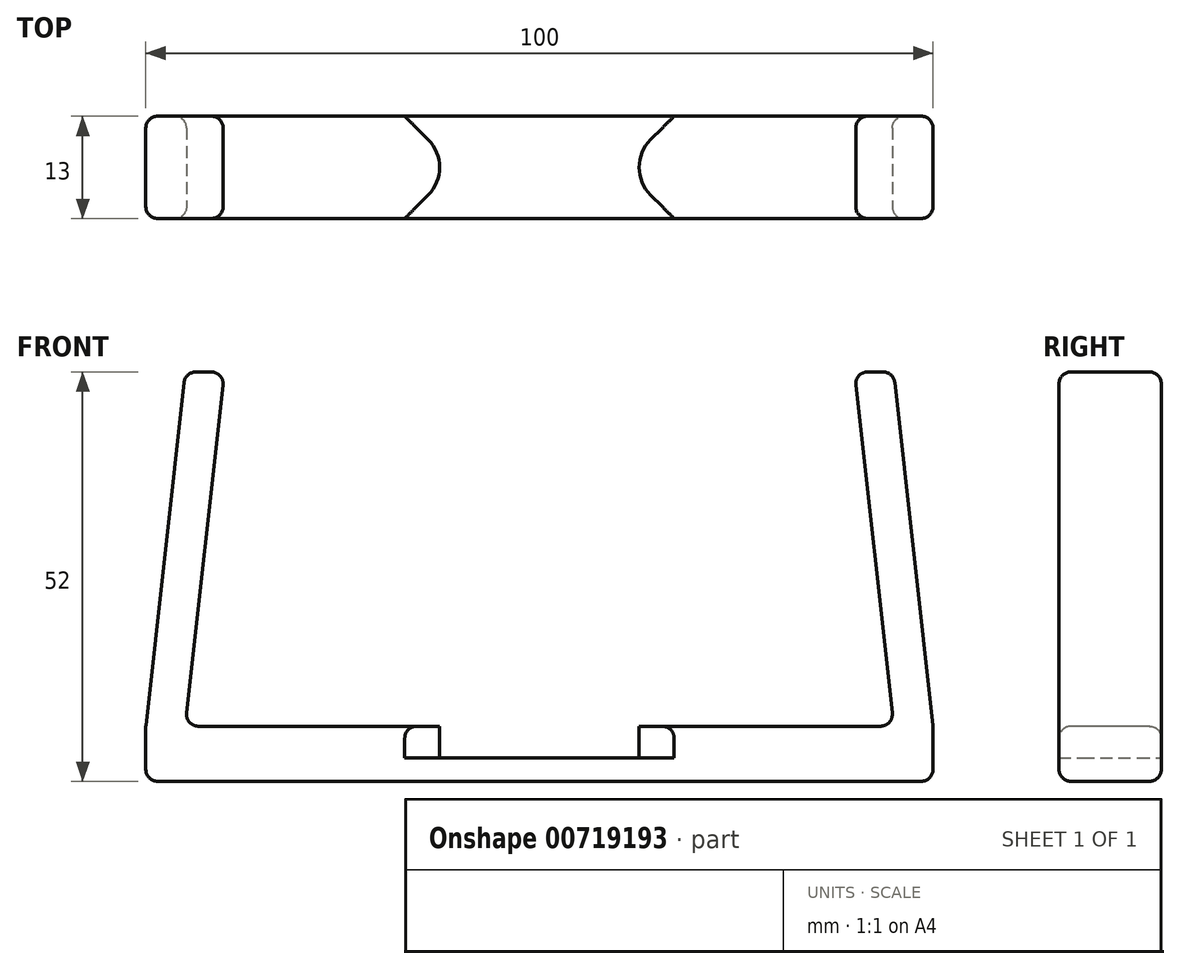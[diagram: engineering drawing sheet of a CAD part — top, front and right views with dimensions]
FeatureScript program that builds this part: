
annotation { "Feature Type Name" : "Feature", "Feature Type Description" : "" }
export const myFeature = defineFeature(function(context is Context, id is Id, definition is map)
    precondition{}
    {
        {
            var Q0;
            Q0=qCreatedBy(makeId("Top.planeOp"),FACE);
            var sketch = newSketch(context, id + "F0", { "sketchPlane" : qUnion([Q0])});
            skLineSegment(sketch, "E0", {"start": v(-45, 0) * mm, "end": v(0, 0) * mm});
            skLineSegment(sketch, "E1", {"start": v(0, 0) * mm, "end": v(45, 0) * mm});
            skLineSegment(sketch, "E2", {"start": v(45, 7) * mm, "end": v(-45, 7) * mm});
            skLineSegment(sketch, "E3", {"start": v(-45, 0) * mm, "end": v(-40, -45) * mm});
            skLineSegment(sketch, "E4", {"start": v(-45, 0) * mm, "end": v(-50, 0) * mm, "construction": true});
            skLineSegment(sketch, "E5", {"start": v(-45, -45) * mm, "end": v(-40, -45) * mm});
            skLineSegment(sketch, "E6", {"start": v(-45, 0) * mm, "end": v(-45, -45) * mm, "construction": true});
            skLineSegment(sketch, "E7", {"start": v(45, 0) * mm, "end": v(45, -45) * mm, "construction": true});
            skLineSegment(sketch, "E8", {"start": v(-45, -45) * mm, "end": v(-50, 0) * mm});
            skLineSegment(sketch, "E9", {"start": v(-45, 7) * mm, "end": v(-44.86, 7) * mm});
            skLineSegment(sketch, "E10", {"start": v(45, 0) * mm, "end": v(50, 0) * mm, "construction": true});
            skLineSegment(sketch, "E11", {"start": v(45, -45) * mm, "end": v(40, -45) * mm});
            skLineSegment(sketch, "E12", {"start": v(40, -45) * mm, "end": v(45, 0) * mm});
            skLineSegment(sketch, "E13", {"start": v(45, -45) * mm, "end": v(50, 0) * mm});
            skLineSegment(sketch, "E14", {"start": v(45, 7) * mm, "end": v(44.86, 7) * mm});
            skLineSegment(sketch, "E15", {"start": v(-45, 7) * mm, "end": v(-50, 7) * mm});
            skLineSegment(sketch, "E16", {"start": v(-50, 7) * mm, "end": v(-50, 0) * mm});
            skLineSegment(sketch, "E17", {"start": v(45, 7) * mm, "end": v(50, 7) * mm});
            skLineSegment(sketch, "E18", {"start": v(50, 7) * mm, "end": v(50, 0) * mm});
            skSolve(sketch);
        }
        {
            var Q0;
            Q0=makeQuery(id+"F0.imprint","IMPRINT",FACE,{"disambiguationData":[TD([[makeQuery(id+"F0.imprint","IMPRINT",EDGE,{"derivedFrom":sQuery(id+"F0.wireOp",EDGE,"E0")}),1.0]])]});
            extrude(context, id + "F1", {"entities" : qUnion([Q0]), "depth" : 13 * mm, "offsetDistance" : 25 * mm});
        }
        {
            var Q0;
            Q0=makeQuery(id+"F1.opExtrude","CAP_FACE",FACE,{"disambiguationData":[OSD([sQuery(id+"F0.wireOp",EDGE,"E0"),sQuery(id+"F0.wireOp",EDGE,"E1"),sQuery(id+"F0.wireOp",EDGE,"E2"),sQuery(id+"F0.wireOp",EDGE,"E3"),sQuery(id+"F0.wireOp",EDGE,"E5"),sQuery(id+"F0.wireOp",EDGE,"E8"),sQuery(id+"F0.wireOp",EDGE,"Ei5dAycY-U04N-QNVS-FxfM-leiImYwHhBUw"),sQuery(id+"F0.wireOp",EDGE,"E9"),sQuery(id+"F0.wireOp",EDGE,"E11"),sQuery(id+"F0.wireOp",EDGE,"E12"),sQuery(id+"F0.wireOp",EDGE,"E13"),sQuery(id+"F0.wireOp",EDGE,"bxxvrJmA-3vw7-joxP-qykT-Xkya98BZcnqR"),sQuery(id+"F0.wireOp",EDGE,"E14"),sQuery(id+"F0.wireOp",EDGE,"5c301a44-3c42-4d68-9b4d-ccadcf804807.filletArc"),sQuery(id+"F0.wireOp",EDGE,"d239349f-1272-4d03-a31e-ecebd73c23f7.filletArc")])],"isStart":false});
            var Q1;
            Q1=makeQuery(id+"F1.opExtrude","CAP_FACE",FACE,{"disambiguationData":[OSD([sQuery(id+"F0.wireOp",EDGE,"E0"),sQuery(id+"F0.wireOp",EDGE,"E1"),sQuery(id+"F0.wireOp",EDGE,"E2"),sQuery(id+"F0.wireOp",EDGE,"E3"),sQuery(id+"F0.wireOp",EDGE,"E5"),sQuery(id+"F0.wireOp",EDGE,"E8"),sQuery(id+"F0.wireOp",EDGE,"Ei5dAycY-U04N-QNVS-FxfM-leiImYwHhBUw"),sQuery(id+"F0.wireOp",EDGE,"E9"),sQuery(id+"F0.wireOp",EDGE,"E11"),sQuery(id+"F0.wireOp",EDGE,"E12"),sQuery(id+"F0.wireOp",EDGE,"E13"),sQuery(id+"F0.wireOp",EDGE,"bxxvrJmA-3vw7-joxP-qykT-Xkya98BZcnqR"),sQuery(id+"F0.wireOp",EDGE,"E14"),sQuery(id+"F0.wireOp",EDGE,"5c301a44-3c42-4d68-9b4d-ccadcf804807.filletArc"),sQuery(id+"F0.wireOp",EDGE,"d239349f-1272-4d03-a31e-ecebd73c23f7.filletArc")])],"isStart":true});
            var Q2;
            Q2=makeQuery(id+"F1.opExtrude","SWEPT_FACE",FACE,{"disambiguationData":[OSD([sQuery(id+"F0.wireOp",EDGE,"E11")])]});
            var Q3;
            Q3=makeQuery(id+"F1.opExtrude","SWEPT_FACE",FACE,{"disambiguationData":[OSD([sQuery(id+"F0.wireOp",EDGE,"E5")])]});
            var Q4;
            Q4=makeQuery(id+"F1.opExtrude","SWEPT_EDGE",EDGE,{"disambiguationData":[OSD([sQuery(id+"F0.wireOp",EDGE,"E0"),sQuery(id+"F0.wireOp",EDGE,"E3")])]});
            var Q5;
            Q5=makeQuery(id+"F1.opExtrude","SWEPT_EDGE",EDGE,{"disambiguationData":[OSD([sQuery(id+"F0.wireOp",EDGE,"E1"),sQuery(id+"F0.wireOp",EDGE,"E12")])]});
            var Q6;
            Q6=makeQuery(id+"F1.opExtrude","SWEPT_EDGE",EDGE,{"disambiguationData":[OSD([sQuery(id+"F0.wireOp",EDGE,"E15"),sQuery(id+"F0.wireOp",EDGE,"E16")])]});
            var Q7;
            Q7=makeQuery(id+"F1.opExtrude","SWEPT_EDGE",EDGE,{"disambiguationData":[OSD([sQuery(id+"F0.wireOp",EDGE,"E8"),sQuery(id+"F0.wireOp",EDGE,"E16")])]});
            var Q8;
            Q8=makeQuery(id+"F1.opExtrude","SWEPT_FACE",FACE,{"disambiguationData":[OSD([sQuery(id+"F0.wireOp",EDGE,"E18")])]});
            var Q9;
            Q9=makeQuery(id+"F1.opExtrude","SWEPT_EDGE",EDGE,{"disambiguationData":[OSD([sQuery(id+"F0.wireOp",EDGE,"E13"),sQuery(id+"F0.wireOp",EDGE,"E18")])]});
            fillet(context, id + "F2", {"entities" : qUnion([Q0, Q1, Q2, Q3, Q4, Q5, Q6, Q7, Q8, Q9]), "radius" : 1.5 * mm, "tangentPropagation" : true, "allowEdgeOverflow" : false});
        }
        {
            var Q0;
            Q0=makeQuery(id+"F1.opExtrude","SWEPT_FACE",FACE,{"disambiguationData":[OSD([sQuery(id+"F0.wireOp",EDGE,"E0"),sQuery(id+"F0.wireOp",EDGE,"E1")])]});
            var sketch = newSketch(context, id + "F3", { "sketchPlane" : qUnion([Q0])});
            skLineSegment(sketch, "E19", {"start": v(0, 0) * mm, "end": v(6.5, 0) * mm, "construction": true});
            skLineSegment(sketch, "E20", {"start": v(6.5, 0) * mm, "end": v(6.5, 6.5) * mm, "construction": true});
            skLineSegment(sketch, "E21", {"start": v(6.5, 6.5) * mm, "end": v(6.5, 13) * mm, "construction": true});
            skLineSegment(sketch, "E22", {"start": v(6.5, 13) * mm, "end": v(0, 13) * mm, "construction": true});
            skLineSegment(sketch, "E23", {"start": v(0, 13) * mm, "end": v(-6.5, 13) * mm, "construction": true});
            skLineSegment(sketch, "E24", {"start": v(-6.5, 13) * mm, "end": v(-6.5, 6.5) * mm, "construction": true});
            skLineSegment(sketch, "E25", {"start": v(-6.5, 6.5) * mm, "end": v(-6.5, 0) * mm, "construction": true});
            skLineSegment(sketch, "E26", {"start": v(-6.5, 0) * mm, "end": v(0, 0) * mm, "construction": true});
            skLineSegment(sketch, "E27", {"start": v(-6.5, 0) * mm, "end": v(6.5, 13) * mm, "construction": true});
            skLineSegment(sketch, "E28", {"start": v(6.5, 13) * mm, "end": v(19.5, 26) * mm, "construction": true});
            skLineSegment(sketch, "E29", {"start": v(-6.5, 0) * mm, "end": v(-19.5, -13) * mm, "construction": true});
            skLineSegment(sketch, "E30", {"start": v(-19.5, -13) * mm, "end": v(-24.8, -7.7) * mm});
            skLineSegment(sketch, "E31", {"start": v(-19.5, -13) * mm, "end": v(-14.2, -18.3) * mm});
            skLineSegment(sketch, "E32", {"start": v(24.8, 20.7) * mm, "end": v(19.5, 26) * mm});
            skLineSegment(sketch, "E33", {"start": v(14.2, 31.3) * mm, "end": v(19.5, 26) * mm});
            skLineSegment(sketch, "E34", {"start": v(-6.5, 13) * mm, "end": v(6.5, 0) * mm, "construction": true});
            skLineSegment(sketch, "E35", {"start": v(6.5, 0) * mm, "end": v(19.5, -13) * mm, "construction": true});
            skLineSegment(sketch, "E36", {"start": v(-6.5, 13) * mm, "end": v(-19.5, 26) * mm, "construction": true});
            skLineSegment(sketch, "E37", {"start": v(-19.5, 26) * mm, "end": v(-14.2, 31.3) * mm});
            skLineSegment(sketch, "E38", {"start": v(24.8, -7.7) * mm, "end": v(19.5, -13) * mm});
            skLineSegment(sketch, "E39", {"start": v(19.5, -13) * mm, "end": v(14.2, -18.3) * mm});
            skLineSegment(sketch, "E40", {"start": v(-24.8, 20.7) * mm, "end": v(-19.5, 26) * mm});
            skLineSegment(sketch, "E41", {"start": v(-14.2, 31.3) * mm, "end": v(0, 17.1) * mm});
            skLineSegment(sketch, "E42", {"start": v(0, 17.1) * mm, "end": v(14.2, 31.3) * mm});
            skLineSegment(sketch, "E43", {"start": v(24.8, 20.7) * mm, "end": v(14.14, 10.04) * mm});
            skLineSegment(sketch, "E44", {"start": v(14.14, 2.96) * mm, "end": v(24.8, -7.7) * mm});
            skLineSegment(sketch, "E45", {"start": v(14.2, -18.3) * mm, "end": v(0, -4.1) * mm});
            skLineSegment(sketch, "E46", {"start": v(0, -4.1) * mm, "end": v(-14.2, -18.3) * mm});
            skLineSegment(sketch, "E47", {"start": v(-24.8, -7.7) * mm, "end": v(-14.14, 2.96) * mm});
            skLineSegment(sketch, "E48", {"start": v(-14.14, 10.04) * mm, "end": v(-24.8, 20.7) * mm});
            skPoint(sketch, "E49.visualSharp", {"position": v(-10.6, 6.5) * mm});
            skArc(sketch, "E49.filletArc", {"start": v(-14.14, 2.96) * mm, "mid": v(-12.68, 6.5) * mm, "end": v(-14.14, 10.04) * mm});
            skPoint(sketch, "E50.visualSharp", {"position": v(10.6, 6.5) * mm});
            skArc(sketch, "E50.filletArc", {"start": v(14.14, 10.04) * mm, "mid": v(12.68, 6.5) * mm, "end": v(14.14, 2.96) * mm});
            skSolve(sketch);
        }
        {
            var Q0;
            {var subQ0=sQuery(id+"F3.wireOp",EDGE,"E49.filletArc");Q0=makeQuery(id+"F3.imprint","IMPRINT",FACE,{"disambiguationData":[TD([[makeQuery(id+"F3.imprint","IMPRINT",EDGE,{"derivedFrom":subQ0}),-1.0]])]});}
            var Q1;
            {var subQ8=sQuery(id+"F3.wireOp",EDGE,"E32");Q1=makeQuery(id+"F3.imprint","IMPRINT",FACE,{"disambiguationData":[TD([[makeQuery(id+"F3.imprint","IMPRINT",EDGE,{"derivedFrom":subQ8}),1.0]])]});}
            var Q2;
            {var subQ2=sQuery(id+"F3.wireOp",EDGE,"E30");Q2=makeQuery(id+"F3.imprint","IMPRINT",FACE,{"disambiguationData":[TD([[makeQuery(id+"F3.imprint","IMPRINT",EDGE,{"derivedFrom":subQ2}),-1.0]])]});}
            extrude(context, id + "F4", {"entities" : qUnion([Q0, Q1, Q2]), "operationType" : NewBodyOperationType.REMOVE, "oppositeDirection" : true, "depth" : 4 * mm, "offsetDistance" : 25 * mm});
        }
        {
            var Q0;
            Q0=makeQuery(id+"F1.opExtrude","SWEPT_BODY",BODY,{"disambiguationData":[OSD([sQuery(id+"F0.wireOp",EDGE,"E0"),sQuery(id+"F0.wireOp",EDGE,"E1"),sQuery(id+"F0.wireOp",EDGE,"E2"),sQuery(id+"F0.wireOp",EDGE,"E3"),sQuery(id+"F0.wireOp",EDGE,"E5"),sQuery(id+"F0.wireOp",EDGE,"E8"),sQuery(id+"F0.wireOp",EDGE,"E9"),sQuery(id+"F0.wireOp",EDGE,"E11"),sQuery(id+"F0.wireOp",EDGE,"E12"),sQuery(id+"F0.wireOp",EDGE,"E13"),sQuery(id+"F0.wireOp",EDGE,"E14"),sQuery(id+"F0.wireOp",EDGE,"E15"),sQuery(id+"F0.wireOp",EDGE,"E16"),sQuery(id+"F0.wireOp",EDGE,"E17"),sQuery(id+"F0.wireOp",EDGE,"E18")])]});
            var Q1;
            Q1=makeQuery(id+"F4.boolean.opBoolean","INTERSECT",EDGE,{"derivedFrom":[makeQuery(id+"F1.opExtrude","CAP_FACE",FACE,{"disambiguationData":[OSD([sQuery(id+"F0.wireOp",EDGE,"E0"),sQuery(id+"F0.wireOp",EDGE,"E1"),sQuery(id+"F0.wireOp",EDGE,"E2"),sQuery(id+"F0.wireOp",EDGE,"E3"),sQuery(id+"F0.wireOp",EDGE,"E5"),sQuery(id+"F0.wireOp",EDGE,"E8"),sQuery(id+"F0.wireOp",EDGE,"E9"),sQuery(id+"F0.wireOp",EDGE,"E11"),sQuery(id+"F0.wireOp",EDGE,"E12"),sQuery(id+"F0.wireOp",EDGE,"E13"),sQuery(id+"F0.wireOp",EDGE,"E14"),sQuery(id+"F0.wireOp",EDGE,"E15"),sQuery(id+"F0.wireOp",EDGE,"E16"),sQuery(id+"F0.wireOp",EDGE,"E17"),sQuery(id+"F0.wireOp",EDGE,"E18")])],"isStart":true}),makeQuery(id+"F4.opExtrude","CAP_FACE",FACE,{"disambiguationData":[OSD([sQuery(id+"F3.wireOp",EDGE,"E30"),sQuery(id+"F3.wireOp",EDGE,"E31"),sQuery(id+"F3.wireOp",EDGE,"E32"),sQuery(id+"F3.wireOp",EDGE,"E33"),sQuery(id+"F3.wireOp",EDGE,"E37"),sQuery(id+"F3.wireOp",EDGE,"E38"),sQuery(id+"F3.wireOp",EDGE,"E39"),sQuery(id+"F3.wireOp",EDGE,"E40"),sQuery(id+"F3.wireOp",EDGE,"E41"),sQuery(id+"F3.wireOp",EDGE,"E42"),sQuery(id+"F3.wireOp",EDGE,"E43"),sQuery(id+"F3.wireOp",EDGE,"E44"),sQuery(id+"F3.wireOp",EDGE,"E45"),sQuery(id+"F3.wireOp",EDGE,"E46"),sQuery(id+"F3.wireOp",EDGE,"E47"),sQuery(id+"F3.wireOp",EDGE,"E48"),sQuery(id+"F3.wireOp",EDGE,"E49.filletArc"),sQuery(id+"F3.wireOp",EDGE,"E50.filletArc")])],"isStart":false})]});
            transform(context, id + "F5", {"entities" : qUnion([Q0]), "transformType" : TransformType.ROTATION, "transformAxis" : qUnion([Q1]), "angle" : 90 * degree, "oppositeDirection" : true, "makeCopy" : false});
        }
    });
